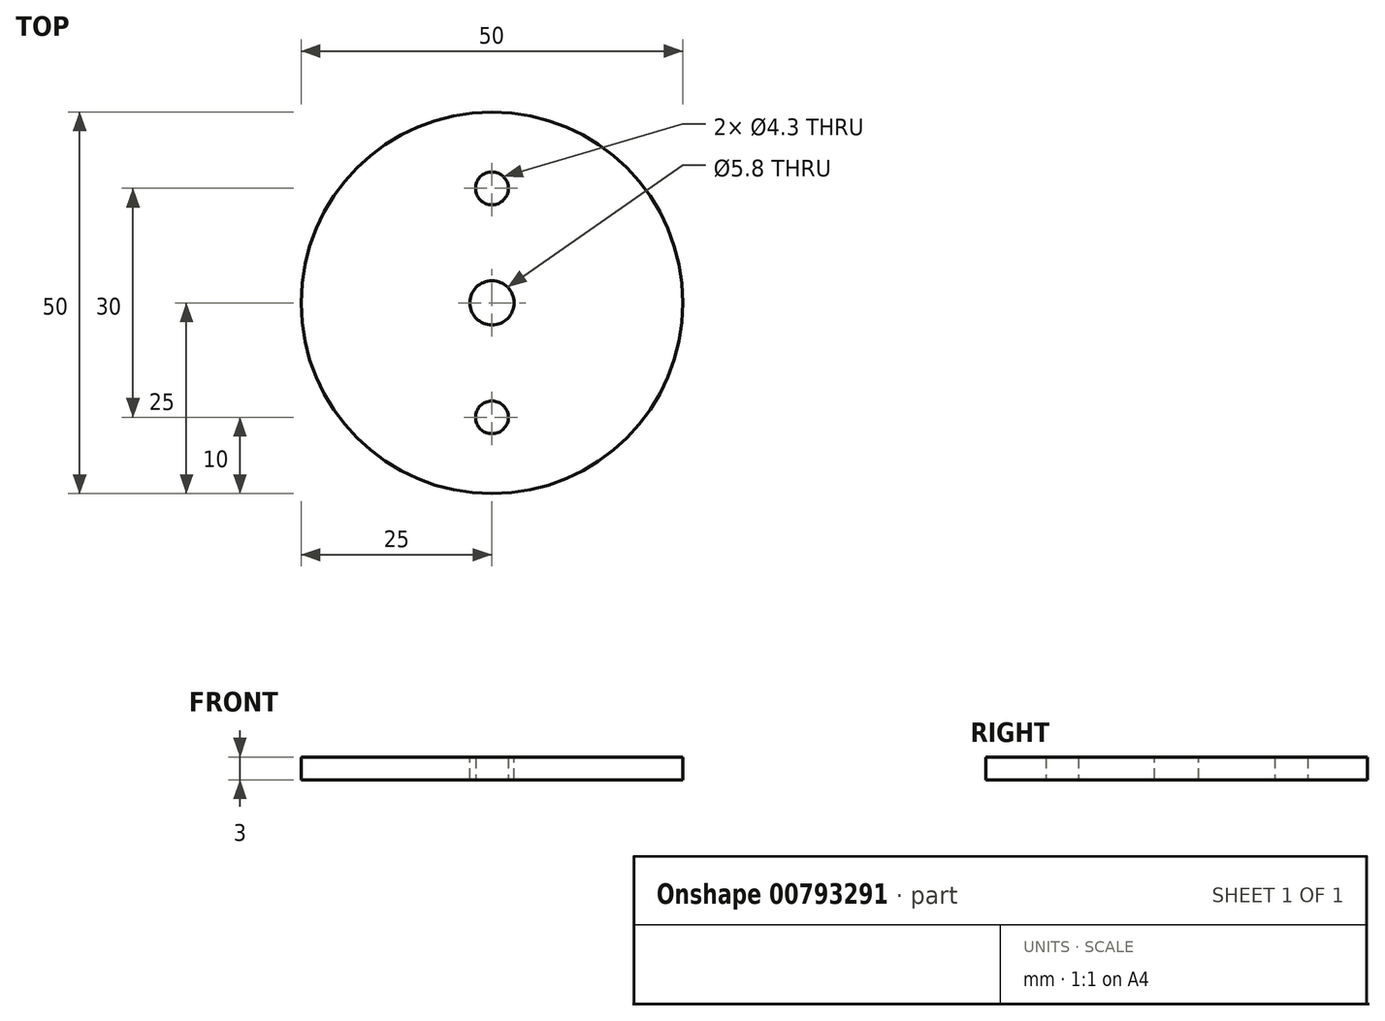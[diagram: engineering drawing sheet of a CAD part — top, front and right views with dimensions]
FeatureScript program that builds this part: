
annotation { "Feature Type Name" : "Feature", "Feature Type Description" : "" }
export const myFeature = defineFeature(function(context is Context, id is Id, definition is map)
    precondition{}
    {
        {
            var Q0;
            Q0=qCreatedBy(makeId("Top.planeOp"),FACE);
            var sketch = newSketch(context, id + "F0", { "sketchPlane" : qUnion([Q0])});
            skCircle(sketch, "E0", {"center": v(0, 0) * mm, "radius": 25 * mm});
            skCircle(sketch, "E1", {"center": v(0, 15) * mm, "radius": 2.15 * mm});
            skCircle(sketch, "E2", {"center": v(0, -15) * mm, "radius": 2.15 * mm});
            skSolve(sketch);
        }
        {
            var Q0;
            Q0 = qSketchRegion(id + "F0", true);
            extrude(context, id + "F1", {"entities" : qUnion([Q0]), "depth" : 3 * mm, "offsetDistance" : 25 * mm});
        }
        {
            var Q0;
            Q0=makeQuery(id+"F1.opExtrude","CAP_FACE",FACE,{"disambiguationData":[OSD([sQuery(id+"F0.wireOp",EDGE,"E0"),sQuery(id+"F0.wireOp",EDGE,"E1"),sQuery(id+"F0.wireOp",EDGE,"E2")])],"isStart":false});
            var sketch = newSketch(context, id + "F2", { "sketchPlane" : qUnion([Q0])});
            skCircle(sketch, "E3", {"center": v(0, 0) * mm, "radius": 2.9 * mm});
            skSolve(sketch);
        }
        {
            var Q0;
            Q0 = qSketchRegion(id + "F2", true);
            extrude(context, id + "F3", {"entities" : qUnion([Q0]), "operationType" : NewBodyOperationType.REMOVE, "endBound" : BoundingType.THROUGH_ALL, "oppositeDirection" : true, "depth" : 25 * mm, "offsetDistance" : 25 * mm});
        }
    });
